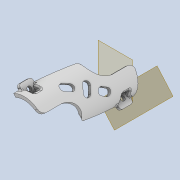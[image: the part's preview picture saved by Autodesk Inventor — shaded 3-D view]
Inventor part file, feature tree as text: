
AUTODESK INVENTOR PART (.ipt)
format: ipt  version: 2020 (Build 240168000, 168)  size: 615,424 bytes
history: native  units: mm
features: sketch x12, extrude x11, fillet x8, projected_geometry x8, reference x7, other x6, plane x4, chamfer x3, thicken_offset x1, hole x1
ambient origin geometry x8: Origin, YZ Plane, XZ Plane, XY Plane, X Axis, Y Axis, Z Axis, Center Point
bodies: Body1 (feature_tree)
feature tree (61):
  plane  "Work Plane1"
  sketch  "Sketch2"  dims[d6=1.5mm d7=1.0mm]
  plane  "Work Plane2"
  extrude  "Extrusion2"  Depth=1.0mm
  extrude  "Extrusion3"  Depth=4.0mm
  extrude  "Extrusion4"  Depth=2.0mm
  extrude  "Extrusion5"  Depth=4.0mm TaperAngle=0.0deg
  chamfer  "Chamfer1"  Distance=4.0mm
  chamfer  "Chamfer2"  Distance=3.0mm Angle=45.0deg
  plane  "Work Plane3"
  plane  "Work Plane4"
  extrude  "Extrusion6"  Depth=5.0mm
  extrude  "Extrusion7"  Depth=1.2mm TaperAngle=0.0deg
  extrude  "Extrusion8"  Depth=1.0mm
  thicken_offset  "Thicken1"
  extrude  "Extrusion9"  Depth=1.0mm
  extrude  "Extrusion10"  Depth=4.0mm TaperAngle=0.0deg
  extrude  "Extrusion11"  Depth=0.2mm
  hole  "Hole1"  [1 undecoded]
  fillet  "Fillet2"  Radius=1.2mm
  fillet  "Fillet3"  Radius=1.2mm
  fillet  "Fillet4"  Radius=1.0mm
  fillet  "Fillet5"  Radius=1.0mm
  fillet  "Fillet6"  Radius=1.0mm
  chamfer  "Chamfer3"  Distance=9.0mm
  fillet  "Fillet7"  Radius=1.0mm
  fillet  "Fillet8"  Radius=1.0mm
  fillet  "Fillet9"  Radius=1.0mm
  extrude  "Extrusion12"  Depth=2.5mm
  reference  "Reference4"
  reference  "Reference5"
  sketch  "Sketch3"  dims[d8=2.0mm d9=4.0mm]
  reference  "Reference6"
  sketch  "Sketch4"  dims[d10=35.0mm d11=0.0mm d12=2.0mm]
  projected_geometry  "Projected Loop1"
  sketch  "Sketch5"  dims[d13=17.5mm d14=0.0mm d15=4.0mm d16=0.0mm d17=4.0mm d18=0.0mm d19=3.0mm d20=14.0mm d21=45.0deg]
  projected_geometry  "Projected Loop2"
  sketch  "Sketch6"  dims[d22=3.0mm d23=14.0mm d24=45.0deg d25=5.0mm]
  reference  "Reference7"
  sketch  "Sketch7"  dims[d26=5.0mm d27=1.2mm d28=0.0mm]
  projected_geometry  "Projected Loop3"
  sketch  "Sketch8"  dims[d29=1.8mm d30=0.0mm d31=1.0mm]
  projected_geometry  "Projected Loop4"
  sketch  "Sketch9"  dims[d32=1.0mm d33=1.0mm]
  reference  "Reference8"
  sketch  "Sketch10"  dims[d34=1.0mm d35=4.0mm d36=0.0mm]
  projected_geometry  "Projected Loop5"
  sketch  "Sketch11"  dims[d37=0.2mm d38=0.2mm]
  projected_geometry  "Projected Loop6"
  sketch  "Sketch12"  dims[d39=5.0mm d40=5.0mm d41=1.2mm d42=0.0mm d43=1.2mm d44=0.0mm d45=1.0mm d46=1.0mm d47=1.0mm]
  reference  "Reference9"
  reference  "Reference10"
  sketch  "Sketch13"  dims[d48=1.0mm d49=9.0mm d50=0.0mm d51=1.6mm d52=6.0mm d53=4.0mm d54=2.0mm d55=90.0deg d56=100.0mm d57=0.0mm d59=1.0mm d60=1.0mm d61=1.0mm d62=0.5mm d63=0.5mm d64=0.5mm d65=14.0mm d66=45.0deg d67=6.0mm d68=1.0mm d69=2.0mm d70=9.0mm d71=9.0mm d72=1.2mm d73=2.5mm d74=1.0mm d75=2.5mm d76=1.0mm d77=2.5mm d78=9.0mm d79=0.0mm]
  projected_geometry  "Projected Loop7"
  projected_geometry  "Projected Loop8"
  parser-record x1  (decoder bookkeeping rows leaked as tree rows — omitted from the tree; the rows remain in map.json)
  other  "tip2_ass_t1.iam"
  other  "bearing_holder_2:1"
  other  "cab_coil_1:2"
  other  "cable_holder_1:1"
  other  "cab_coil_1:1"
note: 1 required parameter value undecoded (feature->parameter linkage not recoverable at this tier; creation-order binding heuristic only, values carry confidence <= 0.55)
note: 1 file-system path scrubbed to <path> (originals preserved in map.json)
